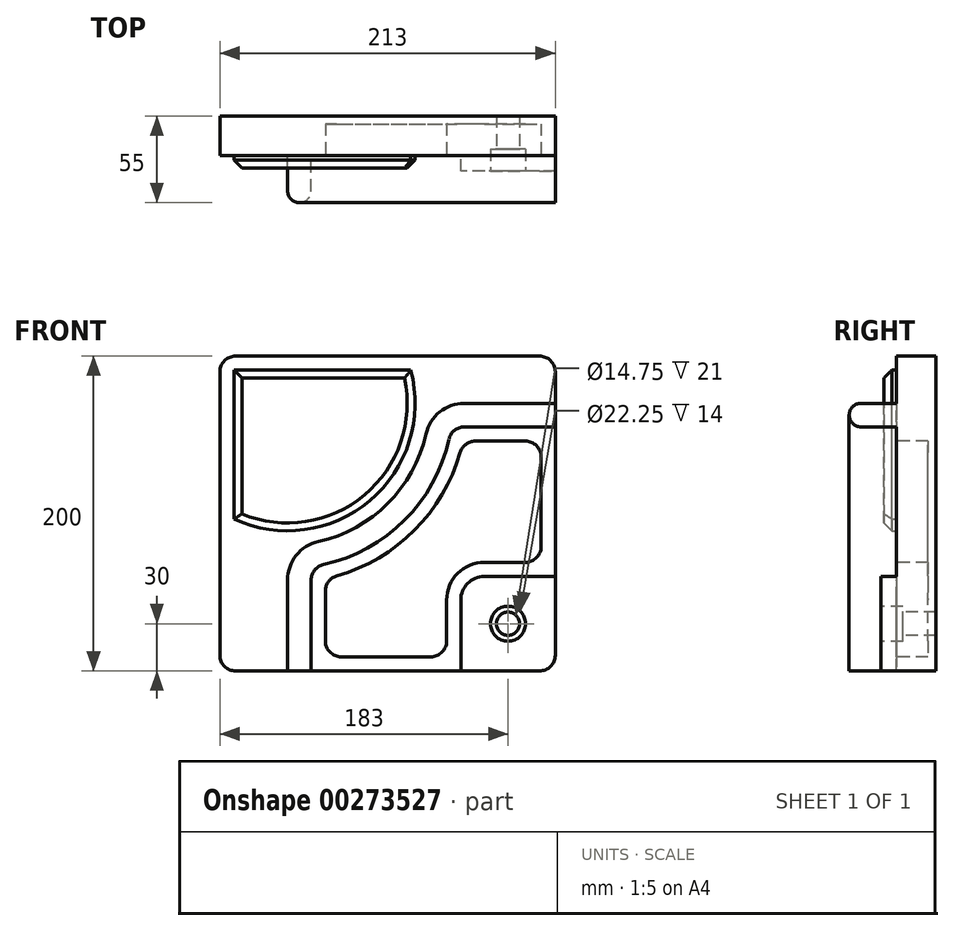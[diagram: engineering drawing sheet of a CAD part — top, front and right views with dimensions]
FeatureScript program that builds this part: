
annotation { "Feature Type Name" : "Feature", "Feature Type Description" : "" }
export const myFeature = defineFeature(function(context is Context, id is Id, definition is map)
    precondition{}
    {
        {
            var Q0;
            Q0=qCreatedBy(makeId("Front.planeOp"),FACE);
            var sketch = newSketch(context, id + "F0", { "sketchPlane" : qUnion([Q0])});
            skLineSegment(sketch, "E0", {"start": v(-96.5, 100) * mm, "end": v(96.5, 100) * mm});
            skLineSegment(sketch, "E1", {"start": v(106.5, 90) * mm, "end": v(106.5, -90) * mm});
            skLineSegment(sketch, "E2", {"start": v(96.5, -100) * mm, "end": v(-96.5, -100) * mm});
            skLineSegment(sketch, "E3", {"start": v(-106.5, 90) * mm, "end": v(-106.5, -90) * mm});
            skPoint(sketch, "E4.visualSharp", {"position": v(-106.5, 100) * mm});
            skArc(sketch, "E4.filletArc", {"start": v(-96.5, 100) * mm, "mid": v(-103.57, 97.07) * mm, "end": v(-106.5, 90) * mm});
            skPoint(sketch, "E5.visualSharp", {"position": v(106.5, 100) * mm});
            skArc(sketch, "E5.filletArc", {"start": v(106.5, 90) * mm, "mid": v(103.57, 97.07) * mm, "end": v(96.5, 100) * mm});
            skPoint(sketch, "E6.visualSharp", {"position": v(106.5, -100) * mm});
            skArc(sketch, "E6.filletArc", {"start": v(96.5, -100) * mm, "mid": v(103.57, -97.07) * mm, "end": v(106.5, -90) * mm});
            skPoint(sketch, "E7.visualSharp", {"position": v(-106.5, -100) * mm});
            skArc(sketch, "E7.filletArc", {"start": v(-106.5, -90) * mm, "mid": v(-103.57, -97.07) * mm, "end": v(-96.5, -100) * mm});
            skPoint(sketch, "E8", {"position": v(76.5, -70) * mm});
            skLineSegment(sketch, "E9", {"start": v(106.5, -40) * mm, "end": v(61.5, -40) * mm});
            skLineSegment(sketch, "E10", {"start": v(46.5, -55) * mm, "end": v(46.5, -100) * mm});
            skPoint(sketch, "E11.visualSharp", {"position": v(46.5, -40) * mm});
            skArc(sketch, "E11.filletArc", {"start": v(61.5, -40) * mm, "mid": v(50.9, -44.4) * mm, "end": v(46.5, -55) * mm});
            skPoint(sketch, "E12", {"position": v(-63.5, 70) * mm});
            skArc(sketch, "E13", {"start": v(-97.5, -3.52) * mm, "mid": v(-11.32, 8.04) * mm, "end": v(14.73, 91) * mm});
            skLineSegment(sketch, "E14", {"start": v(-63.5, -100) * mm, "end": v(-63.5, -42.25) * mm});
            skLineSegment(sketch, "E15", {"start": v(-97.5, 91) * mm, "end": v(14.73, 91) * mm});
            skLineSegment(sketch, "E16", {"start": v(-97.5, 91) * mm, "end": v(-97.5, -3.52) * mm});
            skLineSegment(sketch, "E17", {"start": v(106.5, 70) * mm, "end": v(48.75, 70) * mm});
            skArc(sketch, "E18", {"start": v(-43.93, -17.85) * mm, "mid": v(0.14, 6.36) * mm, "end": v(24.35, 50.43) * mm});
            skPoint(sketch, "E19.visualSharp", {"position": v(26.5, 70) * mm});
            skArc(sketch, "E19.filletArc", {"start": v(48.75, 70) * mm, "mid": v(33.11, 64.5) * mm, "end": v(24.35, 50.43) * mm});
            skPoint(sketch, "E20.visualSharp", {"position": v(-63.5, -20) * mm});
            skArc(sketch, "E20.filletArc", {"start": v(-43.93, -17.85) * mm, "mid": v(-58, -26.61) * mm, "end": v(-63.5, -42.25) * mm});
            skLineSegment(sketch, "E21.0", {"start": v(-48.5, -100) * mm, "end": v(-48.5, -42.25) * mm});
            skLineSegment(sketch, "E21.1", {"start": v(106.5, 55) * mm, "end": v(48.75, 55) * mm});
            skArc(sketch, "E21.2", {"start": v(48.75, 55) * mm, "mid": v(42.5, 52.8) * mm, "end": v(38.99, 47.17) * mm});
            skArc(sketch, "E21.3", {"start": v(-40.67, -32.49) * mm, "mid": v(10.75, -4.25) * mm, "end": v(38.99, 47.17) * mm});
            skArc(sketch, "E21.4", {"start": v(-40.67, -32.49) * mm, "mid": v(-46.3, -36) * mm, "end": v(-48.5, -42.25) * mm});
            skLineSegment(sketch, "E22", {"start": v(-39.5, -81) * mm, "end": v(-39.5, -49.25) * mm});
            skLineSegment(sketch, "E23", {"start": v(87.5, 46) * mm, "end": v(55.75, 46) * mm});
            skLineSegment(sketch, "E24", {"start": v(-29.5, -91) * mm, "end": v(27.5, -91) * mm});
            skLineSegment(sketch, "E25", {"start": v(37.5, -81) * mm, "end": v(37.5, -55) * mm});
            skLineSegment(sketch, "E26", {"start": v(61.5, -31) * mm, "end": v(87.5, -31) * mm});
            skLineSegment(sketch, "E27", {"start": v(97.5, -21) * mm, "end": v(97.5, 36) * mm});
            skArc(sketch, "E28.0", {"start": v(-32.24, -39.63) * mm, "mid": v(17.11, -10.61) * mm, "end": v(46.13, 38.74) * mm});
            skPoint(sketch, "E29.visualSharp", {"position": v(97.5, 46) * mm});
            skArc(sketch, "E29.filletArc", {"start": v(97.5, 36) * mm, "mid": v(94.57, 43.07) * mm, "end": v(87.5, 46) * mm});
            skArc(sketch, "E30.filletArc", {"start": v(55.75, 46) * mm, "mid": v(49.72, 43.98) * mm, "end": v(46.13, 38.74) * mm});
            skArc(sketch, "E31.filletArc", {"start": v(-32.24, -39.63) * mm, "mid": v(-37.48, -43.22) * mm, "end": v(-39.5, -49.25) * mm});
            skPoint(sketch, "E32.visualSharp", {"position": v(-39.5, -91) * mm});
            skArc(sketch, "E32.filletArc", {"start": v(-39.5, -81) * mm, "mid": v(-36.57, -88.07) * mm, "end": v(-29.5, -91) * mm});
            skPoint(sketch, "E33.visualSharp", {"position": v(37.5, -91) * mm});
            skArc(sketch, "E33.filletArc", {"start": v(27.5, -91) * mm, "mid": v(34.57, -88.07) * mm, "end": v(37.5, -81) * mm});
            skPoint(sketch, "E34.visualSharp", {"position": v(97.5, -31) * mm});
            skArc(sketch, "E34.filletArc", {"start": v(87.5, -31) * mm, "mid": v(94.57, -28.07) * mm, "end": v(97.5, -21) * mm});
            skArc(sketch, "E35.0", {"start": v(61.5, -31) * mm, "mid": v(44.53, -38.03) * mm, "end": v(37.5, -55) * mm});
            skSolve(sketch);
        }
        {
            var Q0;
            {var subQ3=sQuery(id+"F0.wireOp",EDGE,"E9");Q0=makeQuery(id+"F0.imprint","IMPRINT",FACE,{"disambiguationData":[TD([[makeQuery(id+"F0.imprint","IMPRINT",EDGE,{"derivedFrom":subQ3}),-1.0]])]});}
            var Q1;
            Q1=makeQuery(id+"F0.imprint","IMPRINT",FACE,{"disambiguationData":[TD([[makeQuery(id+"F0.imprint","IMPRINT",EDGE,{"derivedFrom":sQuery(id+"F0.wireOp",EDGE,"E0")}),-1.0]])]});
            var Q2;
            Q2=makeQuery(id+"F0.imprint","IMPRINT",FACE,{"disambiguationData":[TD([[makeQuery(id+"F0.imprint","IMPRINT",EDGE,{"derivedFrom":sQuery(id+"F0.wireOp",EDGE,"E13")}),1.0]])]});
            var Q3;
            Q3=makeQuery(id+"F0.imprint","IMPRINT",FACE,{"disambiguationData":[TD([[makeQuery(id+"F0.imprint","IMPRINT",EDGE,{"derivedFrom":sQuery(id+"F0.wireOp",EDGE,"E22")}),-1.0]])]});
            var Q4;
            {var subQ0=sQuery(id+"F0.wireOp",EDGE,"E14");Q4=makeQuery(id+"F0.imprint","IMPRINT",FACE,{"disambiguationData":[TD([[makeQuery(id+"F0.imprint","IMPRINT",EDGE,{"derivedFrom":subQ0}),-1.0]])]});}
            var Q5;
            {var subQ1=sQuery(id+"F0.wireOp",EDGE,"E6.filletArc");Q5=makeQuery(id+"F0.imprint","IMPRINT",FACE,{"disambiguationData":[TD([[makeQuery(id+"F0.imprint","IMPRINT",EDGE,{"derivedFrom":subQ1}),1.0]])]});}
            extrude(context, id + "F1", {"entities" : qUnion([Q0, Q1, Q2, Q3, Q4, Q5]), "oppositeDirection" : true, "depth" : 25 * mm});
        }
        {
            var Q0;
            {var subQ1=sQuery(id+"F0.wireOp",EDGE,"E6.filletArc");Q0=makeQuery(id+"F0.imprint","IMPRINT",FACE,{"disambiguationData":[TD([[makeQuery(id+"F0.imprint","IMPRINT",EDGE,{"derivedFrom":subQ1}),1.0]])]});}
            extrude(context, id + "F2", {"entities" : qUnion([Q0]), "operationType" : NewBodyOperationType.ADD, "depth" : 10 * mm});
        }
        {
            var Q0;
            {var subQ0=sQuery(id+"F0.wireOp",EDGE,"E14");Q0=makeQuery(id+"F0.imprint","IMPRINT",FACE,{"disambiguationData":[TD([[makeQuery(id+"F0.imprint","IMPRINT",EDGE,{"derivedFrom":subQ0}),-1.0]])]});}
            extrude(context, id + "F3", {"entities" : qUnion([Q0]), "operationType" : NewBodyOperationType.ADD, "depth" : 30 * mm});
        }
        {
            var Q0;
            Q0=makeQuery(id+"F0.imprint","IMPRINT",FACE,{"disambiguationData":[TD([[makeQuery(id+"F0.imprint","IMPRINT",EDGE,{"derivedFrom":sQuery(id+"F0.wireOp",EDGE,"E22")}),-1.0]])]});
            extrude(context, id + "F4", {"entities" : qUnion([Q0]), "operationType" : NewBodyOperationType.REMOVE, "oppositeDirection" : true, "depth" : 20 * mm});
        }
        {
            var Q0;
            Q0=makeQuery(id+"F0.imprint","IMPRINT",FACE,{"disambiguationData":[TD([[makeQuery(id+"F0.imprint","IMPRINT",EDGE,{"derivedFrom":sQuery(id+"F0.wireOp",EDGE,"E13")}),1.0]])]});
            extrude(context, id + "F5", {"entities" : qUnion([Q0]), "operationType" : NewBodyOperationType.ADD, "depth" : 8 * mm});
        }
        {
            var Q0;
            Q0=makeQuery(id+"F5.opExtrude","CAP_EDGE",EDGE,{"disambiguationData":[OSD([sQuery(id+"F0.wireOp",EDGE,"E15")])],"isStart":false});
            var Q1;
            Q1=makeQuery(id+"F5.opExtrude","CAP_EDGE",EDGE,{"disambiguationData":[OSD([sQuery(id+"F0.wireOp",EDGE,"E16")])],"isStart":false});
            var Q2;
            Q2=makeQuery(id+"F5.opExtrude","CAP_FACE",FACE,{"disambiguationData":[OSD([sQuery(id+"F0.wireOp",EDGE,"E13"),sQuery(id+"F0.wireOp",EDGE,"E15"),sQuery(id+"F0.wireOp",EDGE,"E16")])],"isStart":false});
            chamfer(context, id + "F6", {"entities" : qUnion([Q0, Q1, Q2]), "chamferType" : ChamferType.OFFSET_ANGLE, "width" : 5 * mm, "oppositeDirection" : false, "angle" : 45 * degree, "tangentPropagation" : true});
        }
        {
            var Q0;
            Q0=makeQuery(id+"F2.opExtrude","CAP_FACE",FACE,{"disambiguationData":[OSD([sQuery(id+"F0.wireOp",EDGE,"E1"),sQuery(id+"F0.wireOp",EDGE,"E2"),sQuery(id+"F0.wireOp",EDGE,"E6.filletArc"),sQuery(id+"F0.wireOp",EDGE,"E9"),sQuery(id+"F0.wireOp",EDGE,"E10"),sQuery(id+"F0.wireOp",EDGE,"E11.filletArc")])],"isStart":false});
            var sketch = newSketch(context, id + "F7", { "sketchPlane" : qUnion([Q0])});
            skArc(sketch, "E36.0.0", {"start": v(61.5, -40) * mm, "mid": v(50.9, -44.4) * mm, "end": v(46.5, -55) * mm});
            skLineSegment(sketch, "E36.0.1", {"start": v(46.5, -55) * mm, "end": v(46.5, -100) * mm});
            skLineSegment(sketch, "E36.0.2", {"start": v(46.5, -100) * mm, "end": v(96.5, -100) * mm});
            skArc(sketch, "E36.0.3", {"start": v(96.5, -100) * mm, "mid": v(103.57, -97.07) * mm, "end": v(106.5, -90) * mm});
            skLineSegment(sketch, "E36.0.4", {"start": v(106.5, -90) * mm, "end": v(106.5, -40) * mm});
            skLineSegment(sketch, "E36.0.5", {"start": v(106.5, -40) * mm, "end": v(61.5, -40) * mm});
            skPoint(sketch, "E37", {"position": v(76.5, -70) * mm});
            skSolve(sketch);
        }
        {
            var Q0;
            Q0=sQuery(id+"F7.wireOp",VERTEX,"E37");
            var Q1;
            Q1=makeQuery(id+"F1.opExtrude","SWEPT_BODY",BODY,{"disambiguationData":[OSD([sQuery(id+"F0.wireOp",EDGE,"E0"),sQuery(id+"F0.wireOp",EDGE,"E1"),sQuery(id+"F0.wireOp",EDGE,"E2"),sQuery(id+"F0.wireOp",EDGE,"E3"),sQuery(id+"F0.wireOp",EDGE,"E4.filletArc"),sQuery(id+"F0.wireOp",EDGE,"E5.filletArc"),sQuery(id+"F0.wireOp",EDGE,"E6.filletArc"),sQuery(id+"F0.wireOp",EDGE,"E7.filletArc")])]});
            hole(context, id + "F8", {"style" : HoleStyle.C_BORE, "endStyle" : HoleEndStyle.THROUGH, "standardTappedOrClearance" : lookupTablePath({ "standard" : "ISO", "fit" : "Close", "size" : "M14", "type" : "Clearance" }), "standardBlindInLast" : lookupTablePath({ "fit" : "Close", "standard" : "ISO", "size" : "M14", "type" : "Clearance" }), "holeDiameter" : 14.75 * mm, "cBoreDiameter" : 22.25 * mm, "cBoreDepth" : 14 * mm, "tappedDepth" : 12 * mm, "tapClearance" : 3, "locations" : qUnion([Q0]), "scope" : qUnion([Q1])});
        }
        {
            var Q0;
            Q0=makeQuery(id+"F3.opExtrude","CAP_EDGE",EDGE,{"disambiguationData":[OSD([sQuery(id+"F0.wireOp",EDGE,"E21.0")])],"isStart":false});
            var Q1;
            Q1=makeQuery(id+"F3.opExtrude","CAP_EDGE",EDGE,{"disambiguationData":[OSD([sQuery(id+"F0.wireOp",EDGE,"E14")])],"isStart":false});
            fillet(context, id + "F9", {"entities" : qUnion([Q0, Q1]), "radius" : 7.5 * mm, "tangentPropagation" : true, "allowEdgeOverflow" : false});
        }
    });
